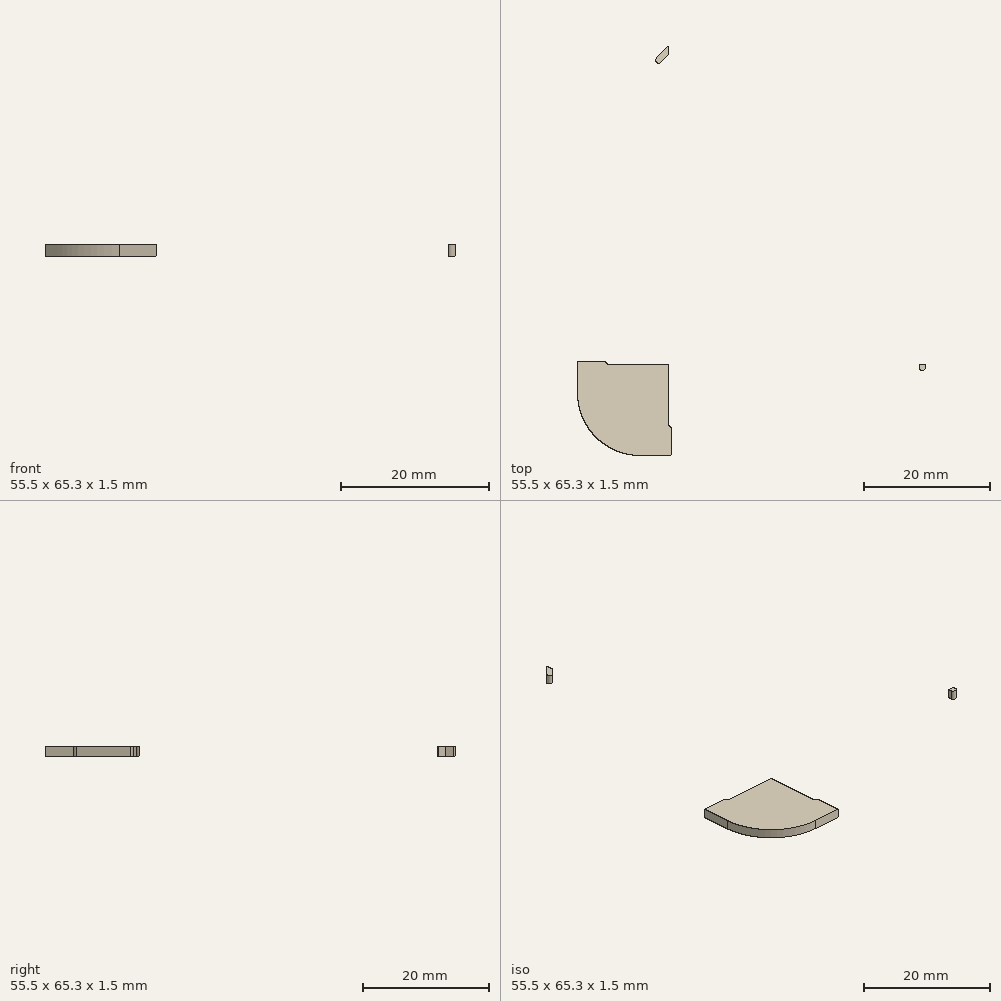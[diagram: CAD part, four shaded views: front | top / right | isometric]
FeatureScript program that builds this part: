
annotation { "Feature Type Name" : "Feature", "Feature Type Description" : "" }
export const myFeature = defineFeature(function(context is Context, id is Id, definition is map)
    precondition{}
    {
        {
            var Q0;
            Q0=qCreatedBy(makeId("Top.planeOp"),FACE);
            var sketch = newSketch(context, id + "F0", { "sketchPlane" : qUnion([Q0])});
            skLineSegment(sketch, "E0", {"start": v(-7.84, 44.32) * mm, "end": v(-7.84, -5.68) * mm});
            skLineSegment(sketch, "E1", {"start": v(-7.84, -5.68) * mm, "end": v(42.16, -5.68) * mm});
            skLineSegment(sketch, "E2", {"start": v(-7.84, -5.68) * mm, "end": v(-7.84, -15.68) * mm});
            skLineSegment(sketch, "E3", {"start": v(-7.84, -15.68) * mm, "end": v(-7.84, -5.68) * mm});
            skLineSegment(sketch, "E4", {"start": v(-17.84, -5.68) * mm, "end": v(-7.84, -5.68) * mm});
            skLineSegment(sketch, "E5", {"start": v(-7.84, 44.32) * mm, "end": v(-7.84, 42.32) * mm});
            skLineSegment(sketch, "E6", {"start": v(-7.84, 44.32) * mm, "end": v(-5.84, 42.32) * mm});
            skLineSegment(sketch, "E7", {"start": v(-7.84, 42.32) * mm, "end": v(-5.84, 42.32) * mm, "construction": true});
            skLineSegment(sketch, "E8.MirrorCS", {"start": v(-7.84, 44.32) * mm, "end": v(-9.84, 42.32) * mm});
            skLineSegment(sketch, "E9", {"start": v(42.16, -5.68) * mm, "end": v(40.16, -5.68) * mm});
            skLineSegment(sketch, "E10", {"start": v(40.16, -5.68) * mm, "end": v(40.16, -7.68) * mm, "construction": true});
            skLineSegment(sketch, "E11", {"start": v(40.16, -7.68) * mm, "end": v(42.16, -5.68) * mm});
            skLineSegment(sketch, "E12.MirrorCS", {"start": v(40.16, -3.68) * mm, "end": v(42.16, -5.68) * mm});
            skLineSegment(sketch, "E13", {"start": v(-7.84, -5.68) * mm, "end": v(-17.84, -5.68) * mm});
            skLineSegment(sketch, "E14", {"start": v(-7.84, -5.68) * mm, "end": v(2.16, -5.68) * mm});
            skLineSegment(sketch, "E15", {"start": v(2.16, -5.68) * mm, "end": v(12.16, -5.68) * mm});
            skLineSegment(sketch, "E16", {"start": v(12.16, -5.68) * mm, "end": v(22.16, -5.68) * mm});
            skLineSegment(sketch, "E17", {"start": v(22.16, -5.68) * mm, "end": v(32.16, -5.68) * mm});
            skLineSegment(sketch, "E18", {"start": v(2.16, -5.68) * mm, "end": v(2.16, -6.68) * mm});
            skLineSegment(sketch, "E19", {"start": v(12.16, -5.68) * mm, "end": v(12.16, -6.68) * mm});
            skLineSegment(sketch, "E20", {"start": v(22.16, -5.68) * mm, "end": v(22.16, -6.68) * mm});
            skLineSegment(sketch, "E21", {"start": v(32.16, -5.68) * mm, "end": v(32.16, -6.68) * mm});
            skLineSegment(sketch, "E22", {"start": v(-7.84, -5.68) * mm, "end": v(-7.84, 4.32) * mm});
            skLineSegment(sketch, "E23", {"start": v(-7.84, 4.32) * mm, "end": v(-7.84, 14.32) * mm});
            skLineSegment(sketch, "E24", {"start": v(-7.84, 14.32) * mm, "end": v(-7.84, 24.32) * mm});
            skLineSegment(sketch, "E25", {"start": v(-7.84, 24.32) * mm, "end": v(-7.84, 34.32) * mm});
            skLineSegment(sketch, "E26", {"start": v(-7.84, 34.32) * mm, "end": v(-8.84, 34.32) * mm});
            skLineSegment(sketch, "E27", {"start": v(-7.84, 24.32) * mm, "end": v(-8.84, 24.32) * mm});
            skLineSegment(sketch, "E28", {"start": v(-7.84, 14.32) * mm, "end": v(-8.84, 14.32) * mm});
            skLineSegment(sketch, "E29", {"start": v(-7.84, 4.32) * mm, "end": v(-8.84, 4.32) * mm});
            skArc(sketch, "E30.0.startCap", {"start": v(-8.34, 44.32) * mm, "mid": v(-7.84, 44.82) * mm, "end": v(-7.34, 44.32) * mm});
            skArc(sketch, "E30.0.endCap", {"start": v(-7.34, -5.68) * mm, "mid": v(-7.84, -6.18) * mm, "end": v(-8.34, -5.68) * mm});
            skLineSegment(sketch, "E30.0.left", {"start": v(-7.34, 44.32) * mm, "end": v(-7.34, -5.68) * mm});
            skLineSegment(sketch, "E30.0.right", {"start": v(-8.34, 44.32) * mm, "end": v(-8.34, -5.68) * mm});
            skArc(sketch, "E30.1.startCap", {"start": v(2.16, -6.18) * mm, "mid": v(1.66, -5.68) * mm, "end": v(2.16, -5.18) * mm});
            skArc(sketch, "E30.1.endCap", {"start": v(12.16, -5.18) * mm, "mid": v(12.66, -5.68) * mm, "end": v(12.16, -6.18) * mm});
            skLineSegment(sketch, "E30.1.left", {"start": v(2.16, -5.18) * mm, "end": v(12.16, -5.18) * mm});
            skLineSegment(sketch, "E30.1.right", {"start": v(2.16, -6.18) * mm, "end": v(12.16, -6.18) * mm});
            skArc(sketch, "E30.2.startCap", {"start": v(-7.34, 14.32) * mm, "mid": v(-7.84, 13.82) * mm, "end": v(-8.34, 14.32) * mm});
            skArc(sketch, "E30.2.endCap", {"start": v(-8.34, 24.32) * mm, "mid": v(-7.84, 24.82) * mm, "end": v(-7.34, 24.32) * mm});
            skLineSegment(sketch, "E30.2.left", {"start": v(-8.34, 14.32) * mm, "end": v(-8.34, 24.32) * mm});
            skLineSegment(sketch, "E30.2.right", {"start": v(-7.34, 14.32) * mm, "end": v(-7.34, 24.32) * mm});
            skArc(sketch, "E30.3.startCap", {"start": v(-17.84, -6.18) * mm, "mid": v(-18.34, -5.68) * mm, "end": v(-17.84, -5.18) * mm});
            skArc(sketch, "E30.3.endCap", {"start": v(-7.84, -5.18) * mm, "mid": v(-7.34, -5.68) * mm, "end": v(-7.84, -6.18) * mm});
            skLineSegment(sketch, "E30.3.left", {"start": v(-17.84, -5.18) * mm, "end": v(-7.84, -5.18) * mm});
            skLineSegment(sketch, "E30.3.right", {"start": v(-17.84, -6.18) * mm, "end": v(-7.84, -6.18) * mm});
            skArc(sketch, "E30.4.startCap", {"start": v(-7.34, -15.68) * mm, "mid": v(-7.84, -16.18) * mm, "end": v(-8.34, -15.68) * mm});
            skArc(sketch, "E30.4.endCap", {"start": v(-8.34, -5.68) * mm, "mid": v(-7.84, -5.18) * mm, "end": v(-7.34, -5.68) * mm});
            skLineSegment(sketch, "E30.4.left", {"start": v(-8.34, -15.68) * mm, "end": v(-8.34, -5.68) * mm});
            skLineSegment(sketch, "E30.4.right", {"start": v(-7.34, -15.68) * mm, "end": v(-7.34, -5.68) * mm});
            skArc(sketch, "E30.5.startCap", {"start": v(-7.34, -5.68) * mm, "mid": v(-7.84, -6.18) * mm, "end": v(-8.34, -5.68) * mm});
            skArc(sketch, "E30.5.endCap", {"start": v(-8.34, 4.32) * mm, "mid": v(-7.84, 4.82) * mm, "end": v(-7.34, 4.32) * mm});
            skLineSegment(sketch, "E30.5.left", {"start": v(-8.34, -5.68) * mm, "end": v(-8.34, 4.32) * mm});
            skLineSegment(sketch, "E30.5.right", {"start": v(-7.34, -5.68) * mm, "end": v(-7.34, 4.32) * mm});
            skArc(sketch, "E30.6.startCap", {"start": v(-7.84, -6.18) * mm, "mid": v(-8.34, -5.68) * mm, "end": v(-7.84, -5.18) * mm});
            skArc(sketch, "E30.6.endCap", {"start": v(42.16, -5.18) * mm, "mid": v(42.66, -5.68) * mm, "end": v(42.16, -6.18) * mm});
            skLineSegment(sketch, "E30.6.left", {"start": v(-7.84, -5.18) * mm, "end": v(42.16, -5.18) * mm});
            skLineSegment(sketch, "E30.6.right", {"start": v(-7.84, -6.18) * mm, "end": v(42.16, -6.18) * mm});
            skArc(sketch, "E30.7.startCap", {"start": v(22.16, -6.18) * mm, "mid": v(21.66, -5.68) * mm, "end": v(22.16, -5.18) * mm});
            skArc(sketch, "E30.7.endCap", {"start": v(32.16, -5.18) * mm, "mid": v(32.66, -5.68) * mm, "end": v(32.16, -6.18) * mm});
            skLineSegment(sketch, "E30.7.left", {"start": v(22.16, -5.18) * mm, "end": v(32.16, -5.18) * mm});
            skLineSegment(sketch, "E30.7.right", {"start": v(22.16, -6.18) * mm, "end": v(32.16, -6.18) * mm});
            skArc(sketch, "E30.8.startCap", {"start": v(-7.84, -6.18) * mm, "mid": v(-8.34, -5.68) * mm, "end": v(-7.84, -5.18) * mm});
            skArc(sketch, "E30.8.endCap", {"start": v(42.16, -5.18) * mm, "mid": v(42.66, -5.68) * mm, "end": v(42.16, -6.18) * mm});
            skLineSegment(sketch, "E30.8.left", {"start": v(-7.84, -5.18) * mm, "end": v(42.16, -5.18) * mm});
            skLineSegment(sketch, "E30.8.right", {"start": v(-7.84, -6.18) * mm, "end": v(42.16, -6.18) * mm});
            skArc(sketch, "E30.9.startCap", {"start": v(-8.34, -5.68) * mm, "mid": v(-7.84, -5.18) * mm, "end": v(-7.34, -5.68) * mm});
            skArc(sketch, "E30.9.endCap", {"start": v(-7.34, -15.68) * mm, "mid": v(-7.84, -16.18) * mm, "end": v(-8.34, -15.68) * mm});
            skLineSegment(sketch, "E30.9.left", {"start": v(-7.34, -5.68) * mm, "end": v(-7.34, -15.68) * mm});
            skLineSegment(sketch, "E30.9.right", {"start": v(-8.34, -5.68) * mm, "end": v(-8.34, -15.68) * mm});
            skArc(sketch, "E30.10.startCap", {"start": v(12.16, -6.18) * mm, "mid": v(11.66, -5.68) * mm, "end": v(12.16, -5.18) * mm});
            skArc(sketch, "E30.10.endCap", {"start": v(22.16, -5.18) * mm, "mid": v(22.66, -5.68) * mm, "end": v(22.16, -6.18) * mm});
            skLineSegment(sketch, "E30.10.left", {"start": v(12.16, -5.18) * mm, "end": v(22.16, -5.18) * mm});
            skLineSegment(sketch, "E30.10.right", {"start": v(12.16, -6.18) * mm, "end": v(22.16, -6.18) * mm});
            skArc(sketch, "E30.11.startCap", {"start": v(-7.84, -5.18) * mm, "mid": v(-7.34, -5.68) * mm, "end": v(-7.84, -6.18) * mm});
            skArc(sketch, "E30.11.endCap", {"start": v(-17.84, -6.18) * mm, "mid": v(-18.34, -5.68) * mm, "end": v(-17.84, -5.18) * mm});
            skLineSegment(sketch, "E30.11.left", {"start": v(-7.84, -6.18) * mm, "end": v(-17.84, -6.18) * mm});
            skLineSegment(sketch, "E30.11.right", {"start": v(-7.84, -5.18) * mm, "end": v(-17.84, -5.18) * mm});
            skArc(sketch, "E30.12.startCap", {"start": v(-7.84, -6.18) * mm, "mid": v(-8.34, -5.68) * mm, "end": v(-7.84, -5.18) * mm});
            skArc(sketch, "E30.12.endCap", {"start": v(2.16, -5.18) * mm, "mid": v(2.66, -5.68) * mm, "end": v(2.16, -6.18) * mm});
            skLineSegment(sketch, "E30.12.left", {"start": v(-7.84, -5.18) * mm, "end": v(2.16, -5.18) * mm});
            skLineSegment(sketch, "E30.12.right", {"start": v(-7.84, -6.18) * mm, "end": v(2.16, -6.18) * mm});
            skArc(sketch, "E30.13.startCap", {"start": v(39.8, -4.04) * mm, "mid": v(39.8, -3.33) * mm, "end": v(40.51, -3.33) * mm});
            skArc(sketch, "E30.13.endCap", {"start": v(42.51, -5.33) * mm, "mid": v(42.51, -6.04) * mm, "end": v(41.8, -6.04) * mm});
            skLineSegment(sketch, "E30.13.left", {"start": v(40.51, -3.33) * mm, "end": v(42.51, -5.33) * mm});
            skLineSegment(sketch, "E30.13.right", {"start": v(39.8, -4.04) * mm, "end": v(41.8, -6.04) * mm});
            skArc(sketch, "E30.14.startCap", {"start": v(-8.2, 44.67) * mm, "mid": v(-7.49, 44.67) * mm, "end": v(-7.49, 43.96) * mm});
            skArc(sketch, "E30.14.endCap", {"start": v(-9.49, 41.97) * mm, "mid": v(-10.2, 41.97) * mm, "end": v(-10.2, 42.67) * mm});
            skLineSegment(sketch, "E30.14.left", {"start": v(-7.49, 43.96) * mm, "end": v(-9.49, 41.97) * mm});
            skLineSegment(sketch, "E30.14.right", {"start": v(-8.2, 44.67) * mm, "end": v(-10.2, 42.67) * mm});
            skArc(sketch, "E30.15.startCap", {"start": v(-7.34, 4.32) * mm, "mid": v(-7.84, 3.82) * mm, "end": v(-8.34, 4.32) * mm});
            skArc(sketch, "E30.15.endCap", {"start": v(-8.34, 14.32) * mm, "mid": v(-7.84, 14.82) * mm, "end": v(-7.34, 14.32) * mm});
            skLineSegment(sketch, "E30.15.left", {"start": v(-8.34, 4.32) * mm, "end": v(-8.34, 14.32) * mm});
            skLineSegment(sketch, "E30.15.right", {"start": v(-7.34, 4.32) * mm, "end": v(-7.34, 14.32) * mm});
            skArc(sketch, "E30.16.startCap", {"start": v(-7.34, 24.32) * mm, "mid": v(-7.84, 23.82) * mm, "end": v(-8.34, 24.32) * mm});
            skArc(sketch, "E30.16.endCap", {"start": v(-8.34, 34.32) * mm, "mid": v(-7.84, 34.82) * mm, "end": v(-7.34, 34.32) * mm});
            skLineSegment(sketch, "E30.16.left", {"start": v(-8.34, 24.32) * mm, "end": v(-8.34, 34.32) * mm});
            skLineSegment(sketch, "E30.16.right", {"start": v(-7.34, 24.32) * mm, "end": v(-7.34, 34.32) * mm});
            skArc(sketch, "E30.17.startCap", {"start": v(31.66, -5.68) * mm, "mid": v(32.16, -5.18) * mm, "end": v(32.66, -5.68) * mm});
            skArc(sketch, "E30.17.endCap", {"start": v(32.66, -6.68) * mm, "mid": v(32.16, -7.18) * mm, "end": v(31.66, -6.68) * mm});
            skLineSegment(sketch, "E30.17.left", {"start": v(32.66, -5.68) * mm, "end": v(32.66, -6.68) * mm});
            skLineSegment(sketch, "E30.17.right", {"start": v(31.66, -5.68) * mm, "end": v(31.66, -6.68) * mm});
            skArc(sketch, "E30.18.startCap", {"start": v(-8.34, 44.32) * mm, "mid": v(-7.84, 44.82) * mm, "end": v(-7.34, 44.32) * mm});
            skLineSegment(sketch, "E30.18.left", {"start": v(-7.34, 44.32) * mm, "end": v(-7.34, 42.32) * mm});
            skLineSegment(sketch, "E30.18.right", {"start": v(-8.34, 44.32) * mm, "end": v(-8.34, 42.32) * mm});
            skArc(sketch, "E30.19.startCap", {"start": v(-7.84, 34.82) * mm, "mid": v(-7.34, 34.32) * mm, "end": v(-7.84, 33.82) * mm});
            skArc(sketch, "E30.19.endCap", {"start": v(-8.84, 33.82) * mm, "mid": v(-9.34, 34.32) * mm, "end": v(-8.84, 34.82) * mm});
            skLineSegment(sketch, "E30.19.left", {"start": v(-7.84, 33.82) * mm, "end": v(-8.84, 33.82) * mm});
            skLineSegment(sketch, "E30.19.right", {"start": v(-7.84, 34.82) * mm, "end": v(-8.84, 34.82) * mm});
            skArc(sketch, "E30.20.startCap", {"start": v(40.51, -8.04) * mm, "mid": v(39.8, -8.04) * mm, "end": v(39.8, -7.33) * mm});
            skArc(sketch, "E30.20.endCap", {"start": v(41.8, -5.33) * mm, "mid": v(42.51, -5.33) * mm, "end": v(42.51, -6.04) * mm});
            skLineSegment(sketch, "E30.20.left", {"start": v(39.8, -7.33) * mm, "end": v(41.8, -5.33) * mm});
            skLineSegment(sketch, "E30.20.right", {"start": v(40.51, -8.04) * mm, "end": v(42.51, -6.04) * mm});
            skArc(sketch, "E30.21.startCap", {"start": v(-8.2, 43.96) * mm, "mid": v(-8.2, 44.67) * mm, "end": v(-7.49, 44.67) * mm});
            skArc(sketch, "E30.21.endCap", {"start": v(-5.49, 42.67) * mm, "mid": v(-5.49, 41.97) * mm, "end": v(-6.2, 41.97) * mm});
            skLineSegment(sketch, "E30.21.left", {"start": v(-7.49, 44.67) * mm, "end": v(-5.49, 42.67) * mm});
            skLineSegment(sketch, "E30.21.right", {"start": v(-8.2, 43.96) * mm, "end": v(-6.2, 41.97) * mm});
            skArc(sketch, "E30.22.endCap", {"start": v(40.66, -7.68) * mm, "mid": v(40.16, -8.18) * mm, "end": v(39.66, -7.68) * mm});
            skArc(sketch, "E30.23.endCap", {"start": v(-5.84, 42.82) * mm, "mid": v(-5.34, 42.32) * mm, "end": v(-5.84, 41.82) * mm});
            skArc(sketch, "E30.24.startCap", {"start": v(-7.84, 4.82) * mm, "mid": v(-7.34, 4.32) * mm, "end": v(-7.84, 3.82) * mm});
            skArc(sketch, "E30.24.endCap", {"start": v(-8.84, 3.82) * mm, "mid": v(-9.34, 4.32) * mm, "end": v(-8.84, 4.82) * mm});
            skLineSegment(sketch, "E30.24.left", {"start": v(-7.84, 3.82) * mm, "end": v(-8.84, 3.82) * mm});
            skLineSegment(sketch, "E30.24.right", {"start": v(-7.84, 4.82) * mm, "end": v(-8.84, 4.82) * mm});
            skArc(sketch, "E30.25.startCap", {"start": v(21.66, -5.68) * mm, "mid": v(22.16, -5.18) * mm, "end": v(22.66, -5.68) * mm});
            skArc(sketch, "E30.25.endCap", {"start": v(22.66, -6.68) * mm, "mid": v(22.16, -7.18) * mm, "end": v(21.66, -6.68) * mm});
            skLineSegment(sketch, "E30.25.left", {"start": v(22.66, -5.68) * mm, "end": v(22.66, -6.68) * mm});
            skLineSegment(sketch, "E30.25.right", {"start": v(21.66, -5.68) * mm, "end": v(21.66, -6.68) * mm});
            skArc(sketch, "E30.26.startCap", {"start": v(1.66, -5.68) * mm, "mid": v(2.16, -5.18) * mm, "end": v(2.66, -5.68) * mm});
            skArc(sketch, "E30.26.endCap", {"start": v(2.66, -6.68) * mm, "mid": v(2.16, -7.18) * mm, "end": v(1.66, -6.68) * mm});
            skLineSegment(sketch, "E30.26.left", {"start": v(2.66, -5.68) * mm, "end": v(2.66, -6.68) * mm});
            skLineSegment(sketch, "E30.26.right", {"start": v(1.66, -5.68) * mm, "end": v(1.66, -6.68) * mm});
            skArc(sketch, "E30.27.startCap", {"start": v(-7.84, 14.82) * mm, "mid": v(-7.34, 14.32) * mm, "end": v(-7.84, 13.82) * mm});
            skArc(sketch, "E30.27.endCap", {"start": v(-8.84, 13.82) * mm, "mid": v(-9.34, 14.32) * mm, "end": v(-8.84, 14.82) * mm});
            skLineSegment(sketch, "E30.27.left", {"start": v(-7.84, 13.82) * mm, "end": v(-8.84, 13.82) * mm});
            skLineSegment(sketch, "E30.27.right", {"start": v(-7.84, 14.82) * mm, "end": v(-8.84, 14.82) * mm});
            skArc(sketch, "E30.28.startCap", {"start": v(42.16, -5.18) * mm, "mid": v(42.66, -5.68) * mm, "end": v(42.16, -6.18) * mm});
            skLineSegment(sketch, "E30.28.left", {"start": v(42.16, -6.18) * mm, "end": v(40.16, -6.18) * mm});
            skLineSegment(sketch, "E30.28.right", {"start": v(42.16, -5.18) * mm, "end": v(40.16, -5.18) * mm});
            skArc(sketch, "E30.29.startCap", {"start": v(11.66, -5.68) * mm, "mid": v(12.16, -5.18) * mm, "end": v(12.66, -5.68) * mm});
            skArc(sketch, "E30.29.endCap", {"start": v(12.66, -6.68) * mm, "mid": v(12.16, -7.18) * mm, "end": v(11.66, -6.68) * mm});
            skLineSegment(sketch, "E30.29.left", {"start": v(12.66, -5.68) * mm, "end": v(12.66, -6.68) * mm});
            skLineSegment(sketch, "E30.29.right", {"start": v(11.66, -5.68) * mm, "end": v(11.66, -6.68) * mm});
            skArc(sketch, "E30.30.startCap", {"start": v(-7.84, 24.82) * mm, "mid": v(-7.34, 24.32) * mm, "end": v(-7.84, 23.82) * mm});
            skArc(sketch, "E30.30.endCap", {"start": v(-8.84, 23.82) * mm, "mid": v(-9.34, 24.32) * mm, "end": v(-8.84, 24.82) * mm});
            skLineSegment(sketch, "E30.30.left", {"start": v(-7.84, 23.82) * mm, "end": v(-8.84, 23.82) * mm});
            skLineSegment(sketch, "E30.30.right", {"start": v(-7.84, 24.82) * mm, "end": v(-8.84, 24.82) * mm});
            skLineSegment(sketch, "E31.bottom", {"start": v(-12.84, -20.68) * mm, "end": v(37.16, -20.68) * mm});
            skLineSegment(sketch, "E31.top", {"start": v(-12.84, 49.32) * mm, "end": v(17.16, 49.32) * mm});
            skLineSegment(sketch, "E31.left", {"start": v(-22.84, -10.68) * mm, "end": v(-22.84, 39.32) * mm});
            skLineSegment(sketch, "E31.right", {"start": v(47.16, -10.68) * mm, "end": v(47.16, 19.32) * mm});
            skPoint(sketch, "E32.visualSharp", {"position": v(-22.84, 49.32) * mm});
            skArc(sketch, "E32.filletArc", {"start": v(-12.84, 49.32) * mm, "mid": v(-19.91, 46.39) * mm, "end": v(-22.84, 39.32) * mm});
            skPoint(sketch, "E33.visualSharp", {"position": v(47.16, 49.32) * mm});
            skArc(sketch, "E33.filletArc", {"start": v(47.16, 19.32) * mm, "mid": v(38.37, 40.53) * mm, "end": v(17.16, 49.32) * mm});
            skPoint(sketch, "E34.visualSharp", {"position": v(47.16, -20.68) * mm});
            skArc(sketch, "E34.filletArc", {"start": v(37.16, -20.68) * mm, "mid": v(44.23, -17.75) * mm, "end": v(47.16, -10.68) * mm});
            skPoint(sketch, "E35.visualSharp", {"position": v(-22.84, -20.68) * mm});
            skArc(sketch, "E35.filletArc", {"start": v(-22.84, -10.68) * mm, "mid": v(-19.91, -17.75) * mm, "end": v(-12.84, -20.68) * mm});
            skLineSegment(sketch, "E36", {"start": v(-7.84, 44.32) * mm, "end": v(-7.84, 49.32) * mm});
            skLineSegment(sketch, "E37", {"start": v(42.16, -5.68) * mm, "end": v(47.16, -5.68) * mm});
            skPoint(sketch, "E37.endSnap0", {"position": v(42.66, -5.68) * mm});
            skLineSegment(sketch, "E38", {"start": v(-7.84, -15.68) * mm, "end": v(-7.84, -20.68) * mm});
            skLineSegment(sketch, "E39", {"start": v(-17.84, -5.68) * mm, "end": v(-22.84, -5.68) * mm});
            skPoint(sketch, "E39.endSnap0", {"position": v(-18.34, -5.68) * mm});
            skLineSegment(sketch, "E40.bottom", {"start": v(-10.71, 41.38) * mm, "end": v(-17.71, 41.38) * mm});
            skLineSegment(sketch, "E40.top", {"start": v(-10.71, 34.38) * mm, "end": v(-17.71, 34.38) * mm});
            skLineSegment(sketch, "E40.left", {"start": v(-10.71, 41.38) * mm, "end": v(-10.71, 34.38) * mm});
            skLineSegment(sketch, "E40.right", {"start": v(-17.71, 41.38) * mm, "end": v(-17.71, 34.38) * mm});
            skLineSegment(sketch, "E41.bottom", {"start": v(39.05, -8.94) * mm, "end": v(32.05, -8.94) * mm});
            skLineSegment(sketch, "E41.top", {"start": v(39.05, -15.94) * mm, "end": v(32.05, -15.94) * mm});
            skLineSegment(sketch, "E41.left", {"start": v(39.05, -8.94) * mm, "end": v(39.05, -15.94) * mm});
            skLineSegment(sketch, "E41.right", {"start": v(32.05, -8.94) * mm, "end": v(32.05, -15.94) * mm});
            skCircle(sketch, "E42", {"center": v(17.16, 19.32) * mm, "radius": 20 * mm});
            skCircle(sketch, "E43", {"center": v(17.16, 39.32) * mm, "radius": 0.5 * mm});
            skLineSegment(sketch, "E44", {"start": v(17.16, 39.32) * mm, "end": v(17.16, -0.68) * mm, "construction": true});
            skLineSegment(sketch, "E45", {"start": v(17.16, 19.32) * mm, "end": v(42.6, 19.32) * mm, "construction": true});
            skCircle(sketch, "E46", {"center": v(37.16, 19.32) * mm, "radius": 0.5 * mm});
            skSolve(sketch);
        }
        {
            var Q0;
            {var subQ39=sQuery(id+"F0.wireOp",EDGE,"E30.14.endCap");Q0=makeQuery(id+"F0.imprint","IMPRINT",FACE,{"disambiguationData":[TD([[makeQuery(id+"F0.imprint","IMPRINT",EDGE,{"derivedFrom":subQ39}),1.0]])]});}
            var Q1;
            {var subQ9=sQuery(id+"F0.wireOp",EDGE,"E35.filletArc");Q1=makeQuery(id+"F0.imprint","IMPRINT",FACE,{"disambiguationData":[TD([[makeQuery(id+"F0.imprint","IMPRINT",EDGE,{"derivedFrom":subQ9}),1.0]])]});}
            var Q2;
            {var subQ39=sQuery(id+"F0.wireOp",EDGE,"E30.17.endCap");Q2=makeQuery(id+"F0.imprint","IMPRINT",FACE,{"disambiguationData":[TD([[makeQuery(id+"F0.imprint","IMPRINT",EDGE,{"derivedFrom":subQ39}),1.0]])]});}
            var Q3;
            Q3=makeQuery(id+"F0.imprint","IMPRINT",FACE,{"disambiguationData":[TD([[makeQuery(id+"F0.imprint","IMPRINT",EDGE,{"derivedFrom":sQuery(id+"F0.wireOp",EDGE,"E30.2.right")}),-1.0]])]});
            extrude(context, id + "F1", {"entities" : qUnion([Q0, Q1, Q2, Q3]), "depth" : 1.5 * mm, "offsetDistance" : 25 * mm});
        }
    });
